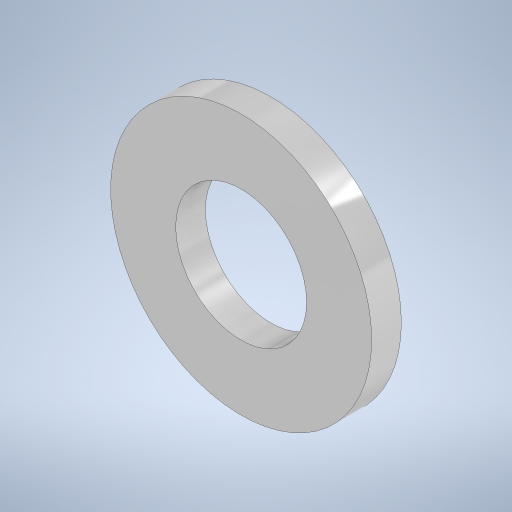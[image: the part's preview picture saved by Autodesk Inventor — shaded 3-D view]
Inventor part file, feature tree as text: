
AUTODESK INVENTOR PART (.ipt)
format: ipt  version: 2024 (Build 280153000, 153)  size: 229,376 bytes
history: native  units: in
note: dims shown in document units (in); Inventor stores cm internally (conversion verified against a paired STEP export)
features: extrude x1, direct_edit x1, sketch x1, other x1
ambient origin geometry x8: Origin, YZ Plane, XZ Plane, XY Plane, X Axis, Y Axis, Z Axis, Center Point
bodies: Solid1 (feature_tree)
feature tree (4):
  extrude  "Extrusion1"  Depth=0.3937in
  direct_edit  "Direct Edit1"
  sketch  "Sketch1"  dims[d0=0.141in d1=0.281in d2=0.032in d3=0.0in d4=3.937in d5=0.3937in d6=0.3937in]
  other  "Scale1"
